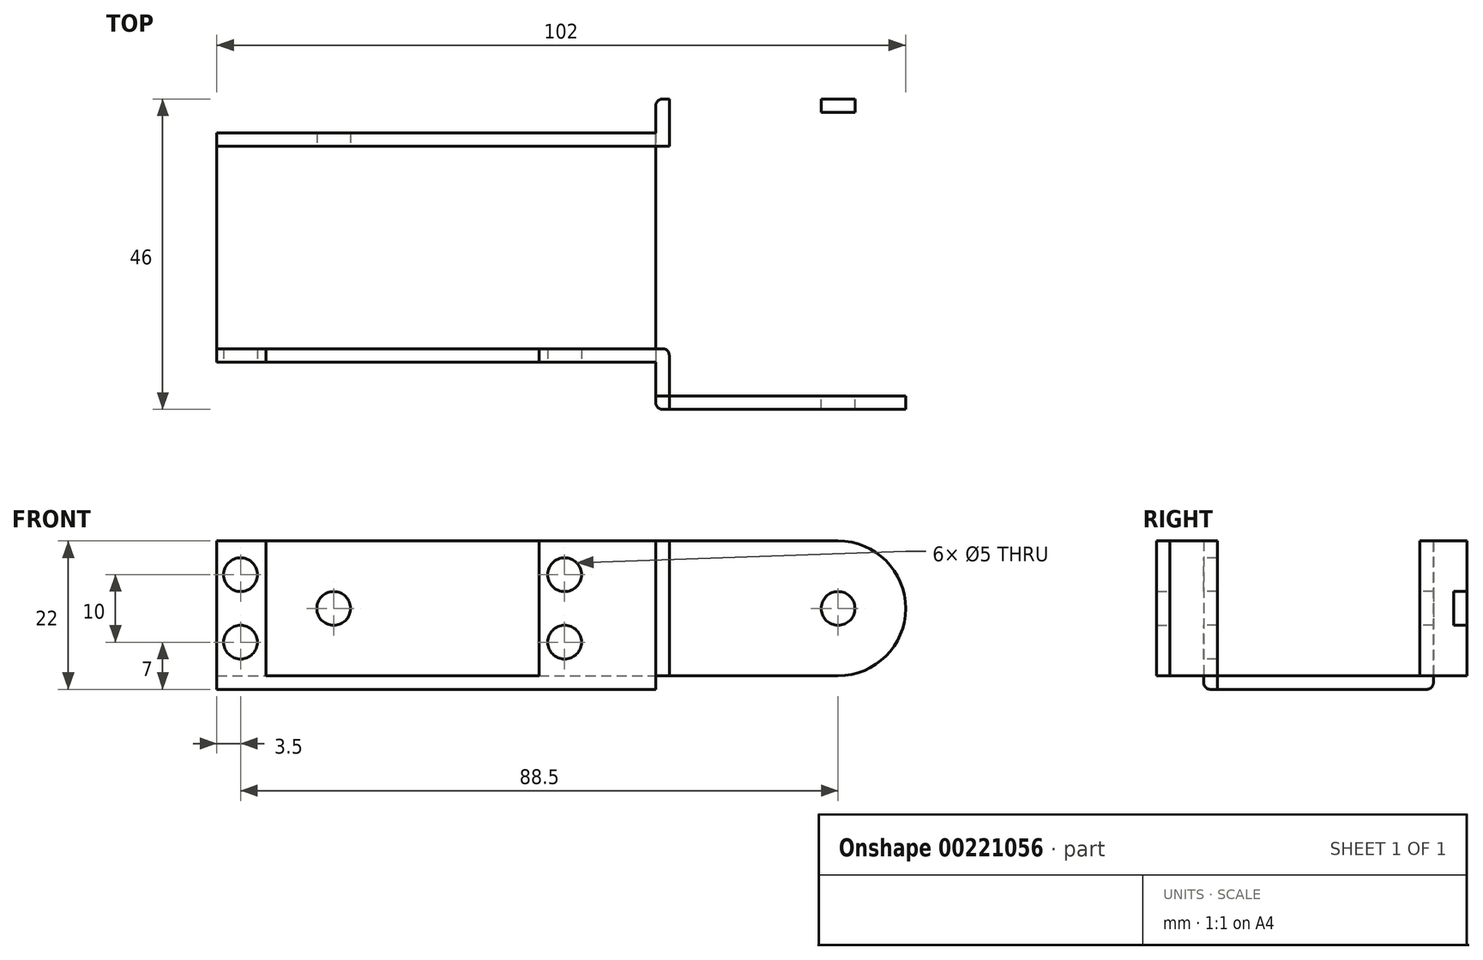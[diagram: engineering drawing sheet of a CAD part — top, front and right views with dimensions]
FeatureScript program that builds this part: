
annotation { "Feature Type Name" : "Feature", "Feature Type Description" : "" }
export const myFeature = defineFeature(function(context is Context, id is Id, definition is map)
    precondition{}
    {
        {
            var Q0;
            Q0=qCreatedBy(makeId("Front.planeOp"),FACE);
            var sketch = newSketch(context, id + "F0", { "sketchPlane" : qUnion([Q0])});
            skLineSegment(sketch, "E0.bottom", {"start": v(-27.5, 10) * mm, "end": v(-20.2, 10) * mm});
            skLineSegment(sketch, "E0.top", {"start": v(-27.5, -10) * mm, "end": v(27.5, -10) * mm});
            skLineSegment(sketch, "E0.left", {"start": v(-27.5, 10) * mm, "end": v(-27.5, -10) * mm});
            skLineSegment(sketch, "E0.right", {"start": v(27.5, 10) * mm, "end": v(27.5, -10) * mm});
            skLineSegment(sketch, "E1", {"start": v(-20.2, 10) * mm, "end": v(-20.2, -10) * mm});
            skLineSegment(sketch, "E2", {"start": v(20.2, 10) * mm, "end": v(20.2, -10) * mm});
            skCircle(sketch, "E3", {"center": v(-24, 5) * mm, "radius": 2.5 * mm});
            skCircle(sketch, "E4", {"center": v(-24, -5) * mm, "radius": 2.5 * mm});
            skCircle(sketch, "E5", {"center": v(24, 5) * mm, "radius": 2.5 * mm});
            skCircle(sketch, "E6", {"center": v(24, -5) * mm, "radius": 2.5 * mm});
            skLineSegment(sketch, "E7", {"start": v(-27.5, -10) * mm, "end": v(-27.5, -12) * mm});
            skLineSegment(sketch, "E8", {"start": v(-27.5, -12) * mm, "end": v(27.5, -12) * mm});
            skLineSegment(sketch, "E9", {"start": v(27.5, -12) * mm, "end": v(27.5, -10) * mm});
            skLineSegment(sketch, "E10.trimOffspring", {"start": v(20.2, 10) * mm, "end": v(27.5, 10) * mm});
            skLineSegment(sketch, "E11", {"start": v(37.5, 10) * mm, "end": v(37.5, -12) * mm});
            skLineSegment(sketch, "E12", {"start": v(37.5, -12) * mm, "end": v(27.5, -12) * mm});
            skLineSegment(sketch, "E13", {"start": v(37.5, 10) * mm, "end": v(39.5, 10) * mm});
            skLineSegment(sketch, "E14", {"start": v(39.5, 10) * mm, "end": v(39.5, -10) * mm});
            skLineSegment(sketch, "E15", {"start": v(27.5, 10) * mm, "end": v(37.5, 10) * mm});
            skLineSegment(sketch, "E16", {"start": v(39.5, -10) * mm, "end": v(37.5, -10) * mm});
            skCircle(sketch, "E17", {"center": v(64.5, 0) * mm, "radius": 2.5 * mm});
            skArc(sketch, "E18", {"start": v(64.5, -10) * mm, "mid": v(74.5, 0) * mm, "end": v(64.5, 10) * mm});
            skLineSegment(sketch, "E19", {"start": v(64.5, 10) * mm, "end": v(39.5, 10) * mm});
            skLineSegment(sketch, "E20", {"start": v(64.5, -10) * mm, "end": v(39.5, -10) * mm});
            skLineSegment(sketch, "E21", {"start": v(27.5, -10) * mm, "end": v(37.5, -10) * mm});
            skSolve(sketch);
        }
        {
            var Q0;
            Q0=qCreatedBy(makeId("Top.planeOp"),FACE);
            var sketch = newSketch(context, id + "F1", { "sketchPlane" : qUnion([Q0])});
            skLineSegment(sketch, "E22", {"start": v(-27.5, 34) * mm, "end": v(-27.5, 2) * mm});
            skLineSegment(sketch, "E23", {"start": v(-27.5, 2) * mm, "end": v(37.5, 2) * mm});
            skLineSegment(sketch, "E24", {"start": v(-27.5, 32) * mm, "end": v(37.5, 32) * mm});
            skLineSegment(sketch, "E25", {"start": v(-27.5, 2) * mm, "end": v(-27.5, 0) * mm});
            skLineSegment(sketch, "E26", {"start": v(-27.5, 0) * mm, "end": v(27.5, 0) * mm});
            skLineSegment(sketch, "E27", {"start": v(-27.5, 34) * mm, "end": v(37.44, 34) * mm});
            skLineSegment(sketch, "E28", {"start": v(37.44, 34) * mm, "end": v(37.44, 32) * mm});
            skLineSegment(sketch, "E29", {"start": v(27.5, 0) * mm, "end": v(37.5, 0) * mm});
            skLineSegment(sketch, "E30", {"start": v(37.5, 0) * mm, "end": v(37.5, 32) * mm});
            skSolve(sketch);
        }
        {
            var Q0;
            {var subQ0=sQuery(id+"F0.wireOp",EDGE,"E13");Q0=makeQuery(id+"F0.imprint","IMPRINT",FACE,{"disambiguationData":[TD([[makeQuery(id+"F0.imprint","IMPRINT",EDGE,{"derivedFrom":subQ0}),-1.0]])]});}
            var Q1;
            Q1=makeQuery(id+"F0.imprint","IMPRINT",FACE,{"disambiguationData":[TD([[makeQuery(id+"F0.imprint","IMPRINT",EDGE,{"derivedFrom":sQuery(id+"F0.wireOp",EDGE,"E0.right")}),1.0]])]});
            var Q2;
            {var subQ0=sQuery(id+"F0.wireOp",EDGE,"E0.right");Q2=makeQuery(id+"F0.imprint","IMPRINT",FACE,{"disambiguationData":[TD([[makeQuery(id+"F0.imprint","IMPRINT",EDGE,{"derivedFrom":subQ0}),-1.0]])]});}
            var Q3;
            Q3=makeQuery(id+"F0.imprint","IMPRINT",FACE,{"disambiguationData":[TD([[makeQuery(id+"F0.imprint","IMPRINT",EDGE,{"derivedFrom":sQuery(id+"F0.wireOp",EDGE,"E9")}),-1.0]])]});
            var Q4;
            {var subQ0=sQuery(id+"F0.wireOp",EDGE,"E7");Q4=makeQuery(id+"F0.imprint","IMPRINT",FACE,{"disambiguationData":[TD([[makeQuery(id+"F0.imprint","IMPRINT",EDGE,{"derivedFrom":subQ0}),1.0]])]});}
            var Q5;
            Q5=makeQuery(id+"F0.imprint","IMPRINT",FACE,{"disambiguationData":[TD([[makeQuery(id+"F0.imprint","IMPRINT",EDGE,{"derivedFrom":sQuery(id+"F0.wireOp",EDGE,"E0.bottom")}),-1.0]])]});
            extrude(context, id + "F2", {"entities" : qUnion([Q0, Q1, Q2, Q3, Q4, Q5]), "oppositeDirection" : true, "depth" : 2 * mm});
        }
        {
            var Q0;
            {var subQ4=sQuery(id+"F1.wireOp",EDGE,"E23");Q0=makeQuery(id+"F1.imprint","IMPRINT",FACE,{"disambiguationData":[TD([[makeQuery(id+"F1.imprint","IMPRINT",EDGE,{"derivedFrom":subQ4}),1.0]])]});}
            extrude(context, id + "F3", {"entities" : qUnion([Q0]), "oppositeDirection" : true, "depth" : 2 * mm});
        }
        {
            var Q0;
            Q0=makeQuery(id+"F3.opExtrude","SWEPT_BODY",BODY,{"disambiguationData":[OSD([sQuery(id+"F1.wireOp",EDGE,"E22"),sQuery(id+"F1.wireOp",EDGE,"E23"),sQuery(id+"F1.wireOp",EDGE,"E24"),sQuery(id+"F1.wireOp",EDGE,"E27"),sQuery(id+"F1.wireOp",EDGE,"E28"),sQuery(id+"F1.wireOp",EDGE,"E30")])]});
            var Q1;
            Q1=makeQuery(id+"F2.opExtrude","CAP_EDGE",EDGE,{"disambiguationData":[OSD([sQuery(id+"F0.wireOp",EDGE,"E0.left"),sQuery(id+"F0.wireOp",EDGE,"E7")])],"isStart":false});
            transform(context, id + "F4", {"entities" : qUnion([Q0]), "transformType" : TransformType.TRANSLATION_DISTANCE, "transformDirection" : qUnion([Q1]), "distance" : 10 * mm, "makeCopy" : false});
        }
        {
            var Q0;
            {var subQ0=sQuery(id+"F0.wireOp",EDGE,"E13");Q0=makeQuery(id+"F0.imprint","IMPRINT",FACE,{"disambiguationData":[TD([[makeQuery(id+"F0.imprint","IMPRINT",EDGE,{"derivedFrom":subQ0}),-1.0]])]});}
            extrude(context, id + "F5", {"entities" : qUnion([Q0]), "operationType" : NewBodyOperationType.ADD, "depth" : 5 * mm});
        }
        {
            var Q0;
            Q0=makeQuery(id+"F0.imprint","IMPRINT",FACE,{"disambiguationData":[TD([[makeQuery(id+"F0.imprint","IMPRINT",EDGE,{"derivedFrom":sQuery(id+"F0.wireOp",EDGE,"E14")}),1.0]])]});
            var Q1;
            Q1=makeQuery(id+"F5.opExtrude","CAP_FACE",FACE,{"disambiguationData":[OSD([sQuery(id+"F0.wireOp",EDGE,"E11"),sQuery(id+"F0.wireOp",EDGE,"E13"),sQuery(id+"F0.wireOp",EDGE,"E14"),sQuery(id+"F0.wireOp",EDGE,"E16")])],"isStart":false});
            extrude(context, id + "F6", {"entities" : qUnion([Q0, Q1]), "depth" : 2 * mm});
        }
        {
            var Q0;
            Q0=makeQuery(id+"F6.opExtrude","SWEPT_BODY",BODY,{"disambiguationData":[OSD([sQuery(id+"F0.wireOp",EDGE,"E14"),sQuery(id+"F0.wireOp",EDGE,"E17"),sQuery(id+"F0.wireOp",EDGE,"E18"),sQuery(id+"F0.wireOp",EDGE,"E19"),sQuery(id+"F0.wireOp",EDGE,"E20")])]});
            var Q1;
            {var subQ0=sQuery(id+"F0.wireOp",EDGE,"E19");var subQ1=sQuery(id+"F0.wireOp",EDGE,"E14");var subQ2=sQuery(id+"F0.wireOp",EDGE,"E13");Q1=makeQuery(id+"F5.boolean.opBoolean","MERGE",EDGE,{"derivedFrom":[makeQuery(id+"F2.opExtrude","SWEPT_EDGE",EDGE,{"disambiguationData":[OSD([subQ2,subQ1,subQ0])]}),makeQuery(id+"F5.opExtrude","SWEPT_EDGE",EDGE,{"disambiguationData":[OSD([subQ2,subQ1,subQ0])]})]});}
            var Q2;
            {var subQ0=sQuery(id+"F0.wireOp",EDGE,"E19");var subQ1=sQuery(id+"F0.wireOp",EDGE,"E14");var subQ2=sQuery(id+"F0.wireOp",EDGE,"E13");Q2=makeQuery(id+"F5.boolean.opBoolean","MERGE",EDGE,{"derivedFrom":[makeQuery(id+"F2.opExtrude","SWEPT_EDGE",EDGE,{"disambiguationData":[OSD([subQ2,subQ1,subQ0])]}),makeQuery(id+"F5.opExtrude","SWEPT_EDGE",EDGE,{"disambiguationData":[OSD([subQ2,subQ1,subQ0])]})]});}
            transform(context, id + "F7", {"entities" : qUnion([Q0]), "transformType" : TransformType.TRANSLATION_DISTANCE, "transformDirection" : qUnion([Q2]), "distance" : 5 * mm, "makeCopy" : false});
        }
        {
            var Q0;
            Q0=makeQuery(id+"F3.opExtrude","SWEPT_FACE",FACE,{"disambiguationData":[OSD([sQuery(id+"F1.wireOp",EDGE,"E24")])]});
            var sketch = newSketch(context, id + "F8", { "sketchPlane" : qUnion([Q0])});
            skCircle(sketch, "E31.MirrorC", {"center": v(-64.5, 0) * mm, "radius": 2.5 * mm});
            skLineSegment(sketch, "E32.MirrorCS", {"start": v(27.5, 10) * mm, "end": v(27.5, -10) * mm});
            skCircle(sketch, "E33", {"center": v(10.2, 0) * mm, "radius": 2.5 * mm});
            skLineSegment(sketch, "E34", {"start": v(-37.5, -10) * mm, "end": v(-37.5, 10) * mm});
            skLineSegment(sketch, "E35", {"start": v(-37.5, 10) * mm, "end": v(-39.5, 10) * mm});
            skLineSegment(sketch, "E36", {"start": v(-39.5, 10) * mm, "end": v(-39.5, -10) * mm});
            skLineSegment(sketch, "E37", {"start": v(-39.5, -10) * mm, "end": v(-37.5, -10) * mm});
            skLineSegment(sketch, "E38", {"start": v(-37.5, -10) * mm, "end": v(-37.5, -12) * mm});
            skLineSegment(sketch, "E39", {"start": v(-37.5, 10) * mm, "end": v(27.5, 10) * mm});
            skLineSegment(sketch, "E40", {"start": v(-39.5, 10) * mm, "end": v(-64.5, 10) * mm});
            skLineSegment(sketch, "E41", {"start": v(-39.5, -10) * mm, "end": v(-64.5, -10) * mm});
            skArc(sketch, "E42", {"start": v(-64.5, 10) * mm, "mid": v(-74.5, 0) * mm, "end": v(-64.5, -10) * mm});
            skSolve(sketch);
        }
        {
            var Q0;
            Q0=makeQuery(id+"F8.imprint","IMPRINT",FACE,{"disambiguationData":[TD([[makeQuery(id+"F8.imprint","IMPRINT",EDGE,{"derivedFrom":sQuery(id+"F8.wireOp",EDGE,"E32.MirrorCS")}),-1.0]])]});
            var Q1;
            Q1=makeQuery(id+"F8.imprint","IMPRINT",FACE,{"disambiguationData":[TD([[makeQuery(id+"F8.imprint","IMPRINT",EDGE,{"derivedFrom":sQuery(id+"F8.wireOp",EDGE,"E38")}),-1.0]])]});
            extrude(context, id + "F9", {"entities" : qUnion([Q0, Q1]), "depth" : 2 * mm});
        }
        {
            var Q0;
            Q0=makeQuery(id+"F8.imprint","IMPRINT",FACE,{"disambiguationData":[TD([[makeQuery(id+"F8.imprint","IMPRINT",EDGE,{"derivedFrom":sQuery(id+"F8.wireOp",EDGE,"E34")}),1.0]])]});
            extrude(context, id + "F10", {"entities" : qUnion([Q0]), "operationType" : NewBodyOperationType.ADD, "depth" : 7 * mm});
        }
        {
            var Q0;
            Q0=makeQuery(id+"F8.imprint","IMPRINT",FACE,{"disambiguationData":[TD([[makeQuery(id+"F8.imprint","IMPRINT",EDGE,{"derivedFrom":sQuery(id+"F8.wireOp",EDGE,"E31.MirrorC")}),1.0]])]});
            extrude(context, id + "F11", {"entities" : qUnion([Q0]), "depth" : 2 * mm});
        }
        {
            var Q0;
            Q0=makeQuery(id+"F11.opExtrude","SWEPT_BODY",BODY,{"disambiguationData":[OSD([sQuery(id+"F8.wireOp",EDGE,"E31.MirrorC"),sQuery(id+"F8.wireOp",EDGE,"E36"),sQuery(id+"F8.wireOp",EDGE,"E40"),sQuery(id+"F8.wireOp",EDGE,"E41"),sQuery(id+"F8.wireOp",EDGE,"xCFFjOfr-ZHEl-xtIQ-mPX2-yJkaWQiFbmXC")])]});
            var Q1;
            Q1=makeQuery(id+"F10.opExtrude","SWEPT_EDGE",EDGE,{"disambiguationData":[OSD([sQuery(id+"F8.wireOp",EDGE,"E35"),sQuery(id+"F8.wireOp",EDGE,"E36"),sQuery(id+"F8.wireOp",EDGE,"E40")])]});
            transform(context, id + "F12", {"entities" : qUnion([Q0]), "transformType" : TransformType.TRANSLATION_DISTANCE, "transformDirection" : qUnion([Q1]), "distance" : 5 * mm, "oppositeDirection" : true, "makeCopy" : false});
        }
        {
            var Q0;
            Q0=makeQuery(id+"F9.opExtrude","CAP_EDGE",EDGE,{"disambiguationData":[OSD([sQuery(id+"F1.wireOp",EDGE,"E24")])],"isStart":false});
            fillet(context, id + "F13", {"entities" : qUnion([Q0]), "radius" : 1 * mm, "tangentPropagation" : true, "allowEdgeOverflow" : false});
        }
        {
            var Q0;
            Q0=makeQuery(id+"F2.opExtrude","CAP_EDGE",EDGE,{"disambiguationData":[OSD([sQuery(id+"F0.wireOp",EDGE,"E8"),sQuery(id+"F0.wireOp",EDGE,"E12")])],"isStart":true});
            fillet(context, id + "F14", {"entities" : qUnion([Q0]), "radius" : 1 * mm, "tangentPropagation" : true, "allowEdgeOverflow" : false});
        }
        {
            var Q0;
            Q0=makeQuery(id+"F2.opExtrude","CAP_EDGE",EDGE,{"disambiguationData":[OSD([sQuery(id+"F0.wireOp",EDGE,"E14")])],"isStart":false});
            fillet(context, id + "F15", {"entities" : qUnion([Q0]), "radius" : 1 * mm, "tangentPropagation" : true, "allowEdgeOverflow" : false});
        }
        {
            var Q0;
            Q0=makeQuery(id+"F10.opExtrude","CAP_EDGE",EDGE,{"disambiguationData":[OSD([sQuery(id+"F8.wireOp",EDGE,"E34")])],"isStart":false});
            fillet(context, id + "F16", {"entities" : qUnion([Q0]), "radius" : 1 * mm, "tangentPropagation" : true, "allowEdgeOverflow" : false});
        }
        {
            var Q0;
            Q0=makeQuery(id+"F6.opExtrude","CAP_EDGE",EDGE,{"disambiguationData":[OSD([sQuery(id+"F0.wireOp",EDGE,"E11")])],"isStart":false});
            fillet(context, id + "F17", {"entities" : qUnion([Q0]), "radius" : 1 * mm, "tangentPropagation" : true, "allowEdgeOverflow" : false});
        }
    });
